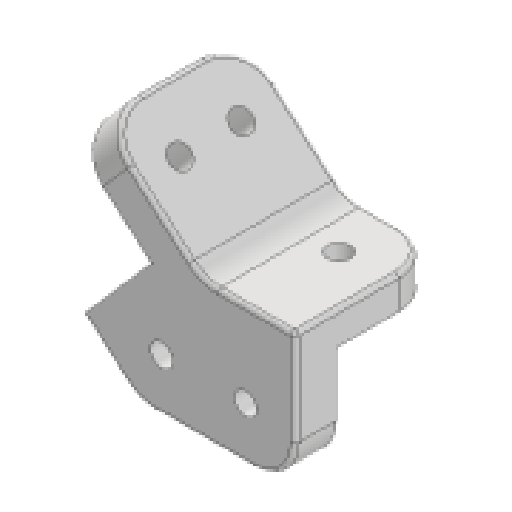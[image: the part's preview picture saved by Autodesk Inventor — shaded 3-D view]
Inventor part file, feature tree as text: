
AUTODESK INVENTOR PART (.ipt)
format: ipt  version: 2025 (Build 290162000, 162)  size: 207,872 bytes
history: native  units: mm
features: extrude x5, sketch x5, reference x4, projected_geometry x3, other x3, fillet x2
ambient origin geometry x8: Origin, YZ Plane, XZ Plane, XY Plane, X Axis, Y Axis, Z Axis, Center Point
bodies: Solid1 (feature_tree)
feature tree (22):
  extrude  "Extrusion1"  Depth=38.1mm
  extrude  "Extrusion2"  Depth=10.0mm TaperAngle=0.0deg
  extrude  "Extrusion3"  Depth=35.4mm TaperAngle=0.0deg
  extrude  "Extrusion5"  Depth=35.4mm TaperAngle=0.0deg
  extrude  "Extrusion6"  TaperAngle=0.0deg  [1 undecoded]
  fillet  "Fillet1"  Radius=10.0mm
  fillet  "Fillet2"  Radius=10.0mm
  sketch  "Sketch1"  dims[d0=25.4mm d1=38.1mm]
  sketch  "Sketch2"  dims[d2=5.5mm d3=10.0mm d4=0.0mm]
  reference  "Reference1"
  reference  "Reference2"
  reference  "Reference3"
  reference  "Reference4"
  sketch  "Sketch3"  dims[d5=10.0mm d6=35.4mm d7=0.0mm]
  projected_geometry  "Projected Loop1"
  sketch  "Sketch5"  dims[d8=8.0mm d9=35.4mm d10=0.0mm]
  projected_geometry  "Projected Loop3"
  sketch  "Sketch6"  dims[d13=5.5mm d14=0.0mm d15=0.0mm d16=10.0mm d17=0.0mm d18=10.0mm d19=1.0mm]
  projected_geometry  "Projected Loop4"
  other  "<userpath>\Desktop\puppycat\woodhouseMK1.iam"
  other  "woodhouseMK1.iam"
  other  "horizontalStrutLower:1"
note: 1 required parameter value undecoded (feature->parameter linkage not recoverable at this tier; creation-order binding heuristic only, values carry confidence <= 0.55)
